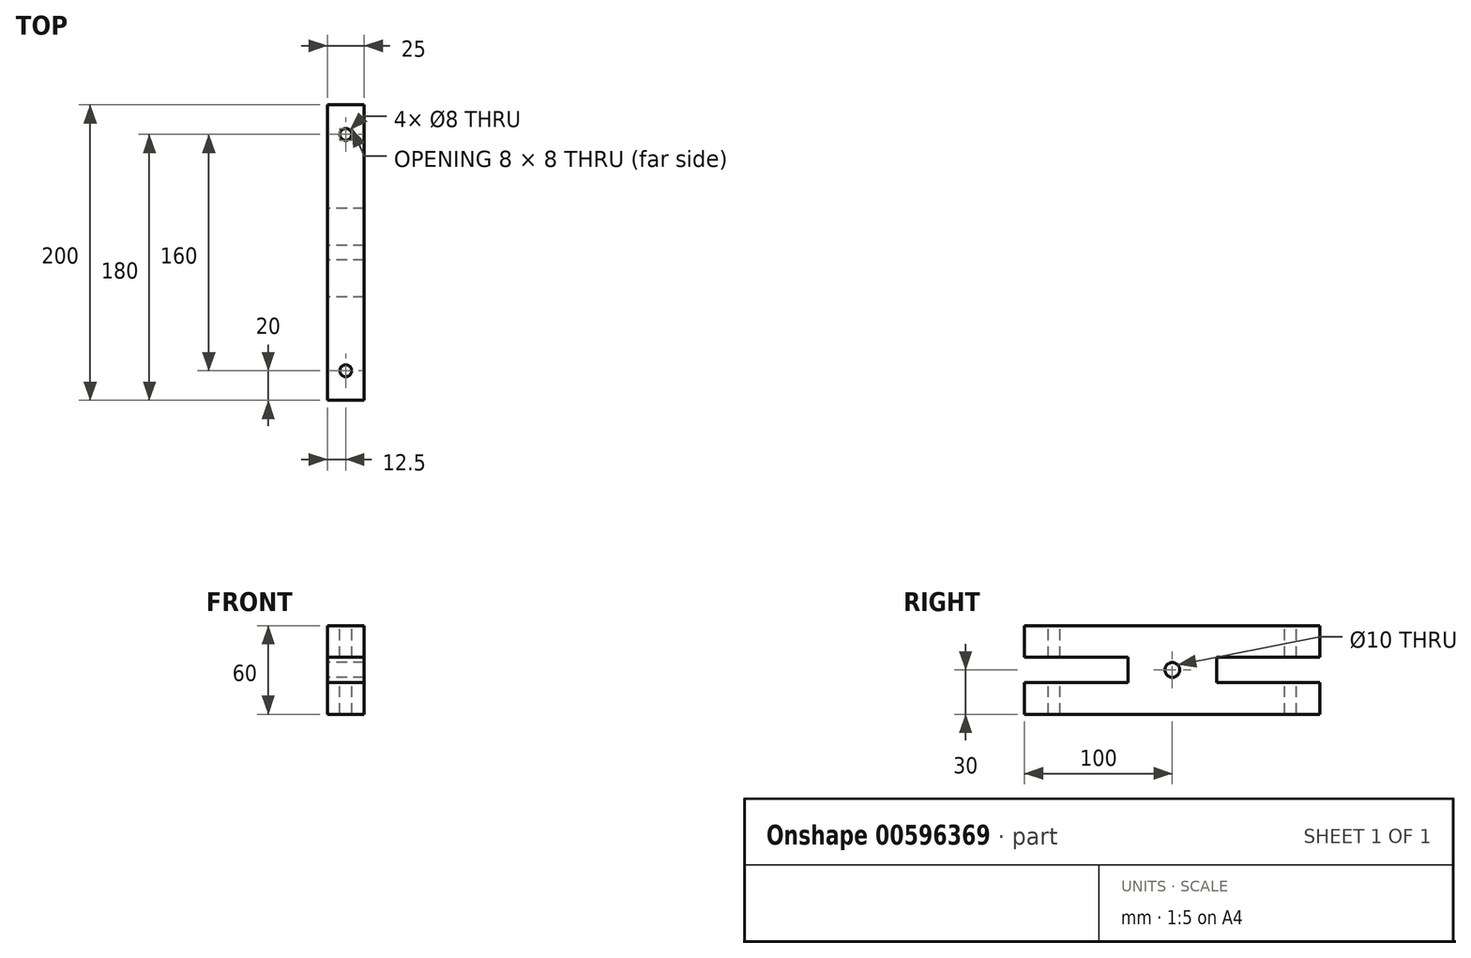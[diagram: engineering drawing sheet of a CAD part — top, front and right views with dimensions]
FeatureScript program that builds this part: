
annotation { "Feature Type Name" : "Feature", "Feature Type Description" : "" }
export const myFeature = defineFeature(function(context is Context, id is Id, definition is map)
    precondition{}
    {
        {
            var Q0;
            Q0=qCreatedBy(makeId("Right.planeOp"),FACE);
            var sketch = newSketch(context, id + "F0", { "sketchPlane" : qUnion([Q0])});
            skLineSegment(sketch, "E0.bottom", {"start": v(100, -30) * mm, "end": v(-100, -30) * mm});
            skLineSegment(sketch, "E0.top", {"start": v(100, 30) * mm, "end": v(-100, 30) * mm});
            skLineSegment(sketch, "E0.left", {"start": v(100, -30) * mm, "end": v(100, -8.5) * mm});
            skLineSegment(sketch, "E0.right", {"start": v(-100, -30) * mm, "end": v(-100, -8.5) * mm});
            skPoint(sketch, "E0.middle", {"position": v(0, 0) * mm});
            skLineSegment(sketch, "E1", {"start": v(-100, 8.5) * mm, "end": v(-30, 8.5) * mm});
            skLineSegment(sketch, "E2", {"start": v(-30, 8.5) * mm, "end": v(-30, -8.5) * mm});
            skLineSegment(sketch, "E3", {"start": v(-30, -8.5) * mm, "end": v(-100, -8.5) * mm});
            skLineSegment(sketch, "E4.trimOffspring", {"start": v(-100, 8.5) * mm, "end": v(-100, 30) * mm});
            skLineSegment(sketch, "E5.MirrorCS", {"start": v(100, 8.5) * mm, "end": v(30, 8.5) * mm});
            skLineSegment(sketch, "E6.MirrorCS", {"start": v(30, 8.5) * mm, "end": v(30, -8.5) * mm});
            skLineSegment(sketch, "E7.MirrorCS", {"start": v(30, -8.5) * mm, "end": v(100, -8.5) * mm});
            skLineSegment(sketch, "E8.trimOffspring", {"start": v(100, 8.5) * mm, "end": v(100, 30) * mm});
            skCircle(sketch, "E9", {"center": v(0, 0) * mm, "radius": 5 * mm});
            skSolve(sketch);
        }
        {
            var Q0;
            Q0=makeQuery(id+"F0.imprint","IMPRINT",FACE,{"disambiguationData":[TD([[makeQuery(id+"F0.imprint","IMPRINT",EDGE,{"derivedFrom":sQuery(id+"F0.wireOp",EDGE,"E0.bottom")}),-1.0]])]});
            extrude(context, id + "F1", {"entities" : qUnion([Q0]), "endBound" : BoundingType.SYMMETRIC, "depth" : 25 * mm, "offsetDistance" : 25 * mm});
        }
        {
            var Q0;
            Q0=makeQuery(id+"F1.opExtrude","SWEPT_FACE",FACE,{"disambiguationData":[OSD([sQuery(id+"F0.wireOp",EDGE,"E0.top")])]});
            var sketch = newSketch(context, id + "F2", { "sketchPlane" : qUnion([Q0])});
            skCircle(sketch, "E10", {"center": v(0, -80) * mm, "radius": 4 * mm});
            skCircle(sketch, "E11", {"center": v(0, 80) * mm, "radius": 4 * mm});
            skSolve(sketch);
        }
        {
            var Q0;
            Q0=sQuery(id+"F2.wireOp",VERTEX,"E10.center");
            var Q1;
            Q1=sQuery(id+"F2.wireOp",VERTEX,"E11.center");
            var Q2;
            Q2=makeQuery(id+"F1.opExtrude","SWEPT_BODY",BODY,{"disambiguationData":[OSD([sQuery(id+"F0.wireOp",EDGE,"E0.bottom"),sQuery(id+"F0.wireOp",EDGE,"E0.top"),sQuery(id+"F0.wireOp",EDGE,"E0.left"),sQuery(id+"F0.wireOp",EDGE,"E0.right"),sQuery(id+"F0.wireOp",EDGE,"E1"),sQuery(id+"F0.wireOp",EDGE,"E2"),sQuery(id+"F0.wireOp",EDGE,"E3"),sQuery(id+"F0.wireOp",EDGE,"E4.trimOffspring"),sQuery(id+"F0.wireOp",EDGE,"E5.MirrorCS"),sQuery(id+"F0.wireOp",EDGE,"E6.MirrorCS"),sQuery(id+"F0.wireOp",EDGE,"E7.MirrorCS"),sQuery(id+"F0.wireOp",EDGE,"E8.trimOffspring"),sQuery(id+"F0.wireOp",EDGE,"E9")])]});
            hole(context, id + "F3", {"style" : HoleStyle.SIMPLE, "endStyle" : HoleEndStyle.THROUGH, "holeDiameter" : 8 * mm, "majorDiameter" : 5 * mm, "isTappedThrough" : true, "tappedDepth" : 12 * mm, "tapClearance" : 3, "locations" : qUnion([Q0, Q1]), "scope" : qUnion([Q2])});
        }
    });
